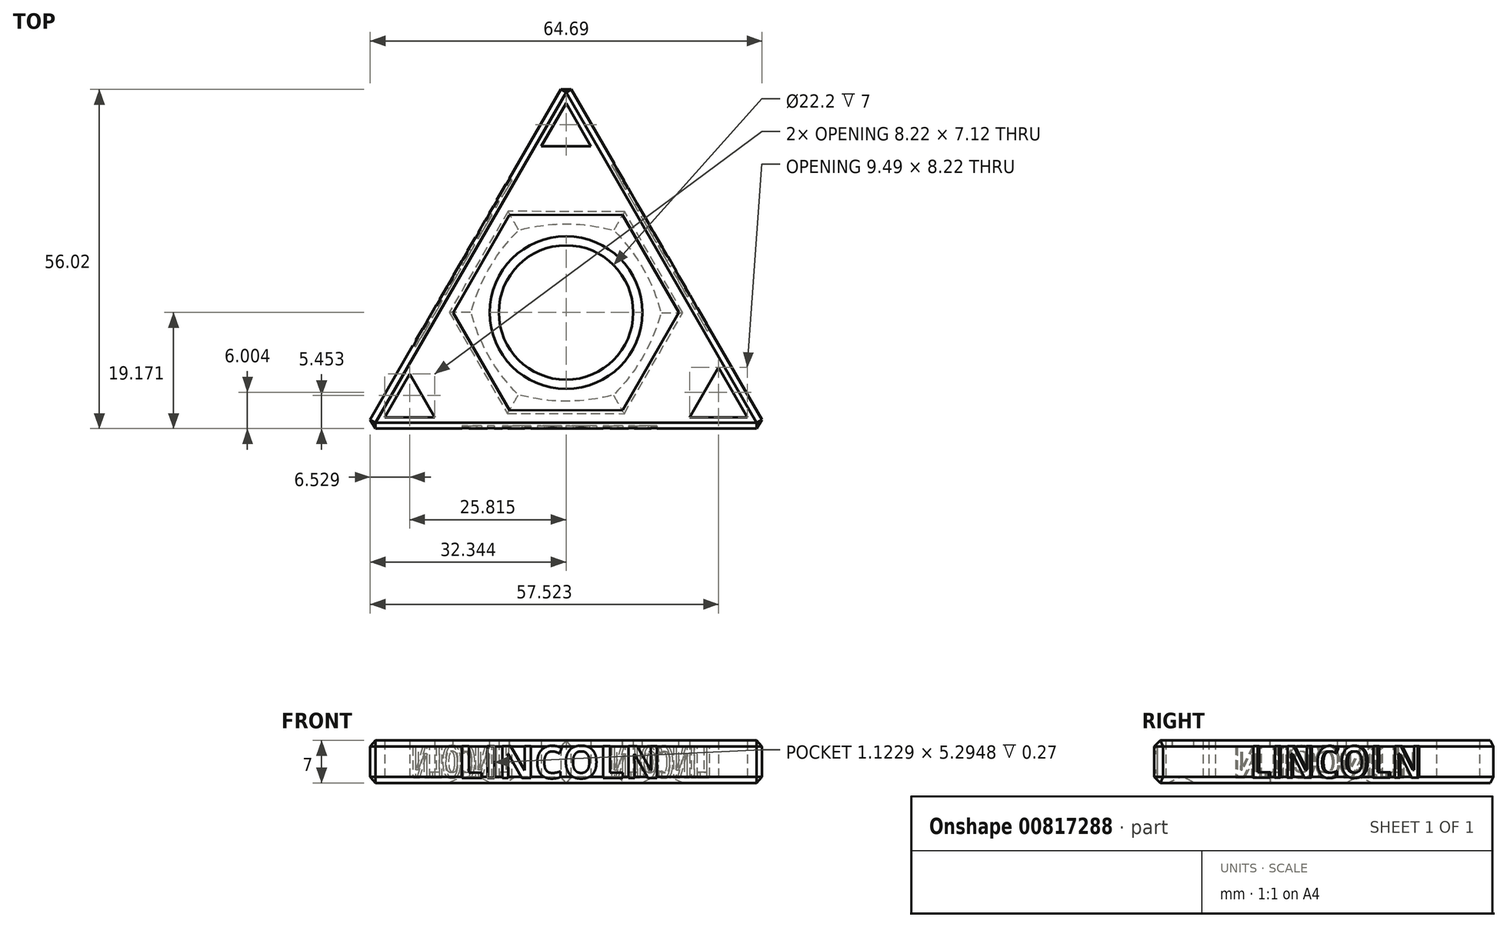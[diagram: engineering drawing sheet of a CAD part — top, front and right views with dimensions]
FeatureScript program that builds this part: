
annotation { "Feature Type Name" : "Feature", "Feature Type Description" : "" }
export const myFeature = defineFeature(function(context is Context, id is Id, definition is map)
    precondition{}
    {
        {
            var Q0;
            Q0=qCreatedBy(makeId("Top.planeOp"),FACE);
            var sketch = newSketch(context, id + "F0", { "sketchPlane" : qUnion([Q0])});
            skLineSegment(sketch, "E0.top", {"start": v(-48.66, -50.6) * mm, "end": v(17.76, -50.6) * mm});
            skLineSegment(sketch, "E1", {"start": v(-48.66, -50.6) * mm, "end": v(-15.45, 6.92) * mm});
            skLineSegment(sketch, "E2", {"start": v(-15.45, 6.92) * mm, "end": v(17.76, -50.6) * mm});
            skCircle(sketch, "E3", {"center": v(-15.45, -31.43) * mm, "radius": 11.1 * mm});
            skPoint(sketch, "E4.start.orphan", {"position": v(-32.05, -21.84) * mm});
            skPoint(sketch, "E5.trimOffspring.end.orphan", {"position": v(-15.45, -50.6) * mm});
            skPoint(sketch, "E6.trimOffspring.end.orphan", {"position": v(0, -21.31) * mm});
            skLineSegment(sketch, "E7.0", {"start": v(-45.37, -48.7) * mm, "end": v(-41.26, -41.59) * mm});
            skLineSegment(sketch, "E8.0", {"start": v(-15.45, 3.12) * mm, "end": v(-11.34, -4) * mm});
            skLineSegment(sketch, "E9.0", {"start": v(-45.37, -48.7) * mm, "end": v(-37.15, -48.7) * mm});
            skLineSegment(sketch, "E10", {"start": v(-37.15, -48.7) * mm, "end": v(-41.26, -41.59) * mm});
            skLineSegment(sketch, "E11", {"start": v(-15.45, -4) * mm, "end": v(-11.34, -4) * mm});
            skLineSegment(sketch, "E12", {"start": v(-15.45, -4) * mm, "end": v(-19.55, -4) * mm});
            skLineSegment(sketch, "E13", {"start": v(7.36, -44.6) * mm, "end": v(9.73, -40.49) * mm});
            skLineSegment(sketch, "E14", {"start": v(7.36, -44.6) * mm, "end": v(4.99, -48.7) * mm});
            skLineSegment(sketch, "E15.trimOffspring", {"start": v(4.99, -48.7) * mm, "end": v(14.48, -48.7) * mm});
            skLineSegment(sketch, "E16.trimOffspring", {"start": v(-19.55, -4) * mm, "end": v(-15.45, 3.12) * mm});
            skLineSegment(sketch, "E17.trimOffspring", {"start": v(9.73, -40.49) * mm, "end": v(14.48, -48.7) * mm});
            skSolve(sketch);
        }
        {
            var Q0;
            Q0=makeQuery(id+"F0.imprint","IMPRINT",FACE,{"disambiguationData":[TD([[makeQuery(id+"F0.imprint","IMPRINT",EDGE,{"derivedFrom":sQuery(id+"F0.wireOp",EDGE,"E0.top")}),1.0]])]});
            extrude(context, id + "F1", {"entities" : qUnion([Q0]), "depth" : 7 * mm, "offsetDistance" : 25 * mm});
        }
        {
            var Q0;
            Q0=makeQuery(id+"F1.opExtrude","SWEPT_FACE",FACE,{"disambiguationData":[OSD([sQuery(id+"F0.wireOp",EDGE,"E0.top")])]});
            var Q1;
            Q1=makeQuery(id+"F1.opExtrude","SWEPT_FACE",FACE,{"disambiguationData":[OSD([sQuery(id+"F0.wireOp",EDGE,"E2")])]});
            var Q2;
            Q2=makeQuery(id+"F1.opExtrude","SWEPT_FACE",FACE,{"disambiguationData":[OSD([sQuery(id+"F0.wireOp",EDGE,"E1")])]});
            chamfer(context, id + "F2", {"entities" : qUnion([Q0, Q1, Q2]), "width" : 1 * mm, "tangentPropagation" : true});
        }
        {
            var Q0;
            Q0=makeQuery(id+"F1.opExtrude","SWEPT_FACE",FACE,{"disambiguationData":[OSD([sQuery(id+"F0.wireOp",EDGE,"E1")])]});
            var sketch = newSketch(context, id + "F3", { "sketchPlane" : qUnion([Q0])});
            skText(sketch, "E18", { "text": "LINCOLN", "fontName": "OpenSans-Bold.ttf"});
            const initialGuessF3  = {"E18": [0.0198, 0.00085, 1, 0, 0.00528]};
            skSetInitialGuess(sketch, initialGuessF3);
            skSolve(sketch);
        }
        {
            var Q0;
            Q0 = qSketchRegion(id + "F3", true);
            extrude(context, id + "F4", {"entities" : qUnion([Q0]), "operationType" : NewBodyOperationType.REMOVE, "oppositeDirection" : true, "depth" : 0.5 * mm, "offsetDistance" : 25 * mm});
        }
        {
            var Q0;
            Q0=makeQuery(id+"F1.opExtrude","SWEPT_FACE",FACE,{"disambiguationData":[OSD([sQuery(id+"F0.wireOp",EDGE,"E0.top")])]});
            var sketch = newSketch(context, id + "F5", { "sketchPlane" : qUnion([Q0])});
            skText(sketch, "E19", { "text": "LINCOLN", "fontName": "OpenSans-Bold.ttf"});
            const initialGuessF5  = {"E19": [-0.0333, 0.00077, 1, 0, 0.00534]};
            skSetInitialGuess(sketch, initialGuessF5);
            skSolve(sketch);
        }
        {
            var Q0;
            Q0 = qSketchRegion(id + "F5", true);
            extrude(context, id + "F6", {"entities" : qUnion([Q0]), "operationType" : NewBodyOperationType.REMOVE, "oppositeDirection" : true, "depth" : 0.5 * mm, "offsetDistance" : 25 * mm});
        }
        {
            var Q0;
            Q0=makeQuery(id+"F1.opExtrude","SWEPT_FACE",FACE,{"disambiguationData":[OSD([sQuery(id+"F0.wireOp",EDGE,"E2")])]});
            var sketch = newSketch(context, id + "F7", { "sketchPlane" : qUnion([Q0])});
            skText(sketch, "E20", { "text": "LINCOLN", "fontName": "OpenSans-Bold.ttf"});
            const initialGuessF7  = {"E20": [-0.0344, 0.00085, 1, 0, 0.00524]};
            skSetInitialGuess(sketch, initialGuessF7);
            skSolve(sketch);
        }
        {
            var Q0;
            Q0 = qSketchRegion(id + "F7", true);
            extrude(context, id + "F8", {"entities" : qUnion([Q0]), "operationType" : NewBodyOperationType.REMOVE, "oppositeDirection" : true, "depth" : 0.5 * mm, "offsetDistance" : 25 * mm});
        }
        {
            var Q0;
            Q0=makeQuery(id+"F1.opExtrude","CAP_FACE",FACE,{"disambiguationData":[OSD([sQuery(id+"F0.wireOp",EDGE,"E0.top"),sQuery(id+"F0.wireOp",EDGE,"E1"),sQuery(id+"F0.wireOp",EDGE,"E2"),sQuery(id+"F0.wireOp",EDGE,"E3"),sQuery(id+"F0.wireOp",EDGE,"E7.0"),sQuery(id+"F0.wireOp",EDGE,"E8.0"),sQuery(id+"F0.wireOp",EDGE,"E9.0"),sQuery(id+"F0.wireOp",EDGE,"E10"),sQuery(id+"F0.wireOp",EDGE,"E11"),sQuery(id+"F0.wireOp",EDGE,"E12"),sQuery(id+"F0.wireOp",EDGE,"E13"),sQuery(id+"F0.wireOp",EDGE,"E14"),sQuery(id+"F0.wireOp",EDGE,"E15.trimOffspring"),sQuery(id+"F0.wireOp",EDGE,"E16.trimOffspring"),sQuery(id+"F0.wireOp",EDGE,"E17.trimOffspring")])],"isStart":false});
            var sketch = newSketch(context, id + "F9", { "sketchPlane" : qUnion([Q0])});
            skCircle(sketch, "E21.0", {"center": v(-15.45, -31.43) * mm, "radius": 12.6 * mm});
            skCircle(sketch, "E22.cCircle", {"center": v(-15.45, -31.43) * mm, "radius": 18.63 * mm, "construction": true});
            skLineSegment(sketch, "E22.0", {"start": v(-6.16, -15.28) * mm, "end": v(3.18, -31.4) * mm});
            skLineSegment(sketch, "E22.1", {"start": v(3.18, -31.4) * mm, "end": v(-6.1, -47.54) * mm});
            skLineSegment(sketch, "E22.2", {"start": v(-6.1, -47.54) * mm, "end": v(-24.73, -47.58) * mm});
            skLineSegment(sketch, "E22.3", {"start": v(-24.73, -47.58) * mm, "end": v(-34.08, -31.47) * mm});
            skLineSegment(sketch, "E22.4", {"start": v(-34.08, -31.47) * mm, "end": v(-24.8, -15.31) * mm});
            skLineSegment(sketch, "E22.5", {"start": v(-24.8, -15.31) * mm, "end": v(-6.16, -15.28) * mm});
            skSolve(sketch);
        }
        {
            var Q0;
            Q0=makeQuery(id+"F9.imprint","IMPRINT",FACE,{"disambiguationData":[TD([[makeQuery(id+"F9.imprint","IMPRINT",EDGE,{"derivedFrom":sQuery(id+"F9.wireOp",EDGE,"E21.0")}),-1.0]])]});
            extrude(context, id + "F10", {"entities" : qUnion([Q0]), "operationType" : NewBodyOperationType.REMOVE, "oppositeDirection" : true, "depth" : 1 * mm, "offsetDistance" : 25 * mm});
        }
        {
            var Q0;
            Q0=makeQuery(id+"F1.opExtrude","CAP_FACE",FACE,{"disambiguationData":[OSD([sQuery(id+"F0.wireOp",EDGE,"E0.top"),sQuery(id+"F0.wireOp",EDGE,"E1"),sQuery(id+"F0.wireOp",EDGE,"E2"),sQuery(id+"F0.wireOp",EDGE,"E3"),sQuery(id+"F0.wireOp",EDGE,"E7.0"),sQuery(id+"F0.wireOp",EDGE,"E8.0"),sQuery(id+"F0.wireOp",EDGE,"E9.0"),sQuery(id+"F0.wireOp",EDGE,"E10"),sQuery(id+"F0.wireOp",EDGE,"E11"),sQuery(id+"F0.wireOp",EDGE,"E12"),sQuery(id+"F0.wireOp",EDGE,"E13"),sQuery(id+"F0.wireOp",EDGE,"E14"),sQuery(id+"F0.wireOp",EDGE,"E15.trimOffspring"),sQuery(id+"F0.wireOp",EDGE,"E16.trimOffspring"),sQuery(id+"F0.wireOp",EDGE,"E17.trimOffspring")])],"isStart":true});
            var sketch = newSketch(context, id + "F11", { "sketchPlane" : qUnion([Q0])});
            skCircle(sketch, "E23.0", {"center": v(-15.45, 31.43) * mm, "radius": 12.6 * mm});
            skCircle(sketch, "E24.cCircle", {"center": v(-15.45, 31.43) * mm, "radius": 19.26 * mm, "construction": true});
            skLineSegment(sketch, "E24.0", {"start": v(-5.86, 48.14) * mm, "end": v(3.82, 31.48) * mm});
            skLineSegment(sketch, "E24.1", {"start": v(3.82, 31.48) * mm, "end": v(-5.77, 14.77) * mm});
            skLineSegment(sketch, "E24.2", {"start": v(-5.77, 14.77) * mm, "end": v(-25.04, 14.72) * mm});
            skLineSegment(sketch, "E24.3", {"start": v(-25.04, 14.72) * mm, "end": v(-34.7, 31.38) * mm});
            skLineSegment(sketch, "E24.4", {"start": v(-34.7, 31.38) * mm, "end": v(-25.12, 48.09) * mm});
            skLineSegment(sketch, "E24.5", {"start": v(-25.12, 48.09) * mm, "end": v(-5.86, 48.14) * mm});
            skSolve(sketch);
        }
        {
            var Q0;
            Q0=makeQuery(id+"F11.imprint","IMPRINT",FACE,{"disambiguationData":[TD([[makeQuery(id+"F11.imprint","IMPRINT",EDGE,{"derivedFrom":sQuery(id+"F11.wireOp",EDGE,"E23.0")}),-1.0]])]});
            extrude(context, id + "F12", {"entities" : qUnion([Q0]), "operationType" : NewBodyOperationType.REMOVE, "oppositeDirection" : true, "depth" : 1 * mm, "offsetDistance" : 25 * mm});
        }
        {
            var Q0;
            Q0=makeQuery(id+"F12.boolean.opBoolean","COPY",FACE,{"derivedFrom":makeQuery(id+"F12.opExtrude","CAP_FACE",FACE,{"disambiguationData":[OSD([sQuery(id+"F11.wireOp",EDGE,"E23.0"),sQuery(id+"F11.wireOp",EDGE,"E24.0"),sQuery(id+"F11.wireOp",EDGE,"E24.1"),sQuery(id+"F11.wireOp",EDGE,"E24.2"),sQuery(id+"F11.wireOp",EDGE,"E24.3"),sQuery(id+"F11.wireOp",EDGE,"E24.4"),sQuery(id+"F11.wireOp",EDGE,"E24.5")])],"isStart":false})});
            fillet(context, id + "F13", {"entities" : qUnion([Q0]), "radius" : 5 * mm, "tangentPropagation" : true, "allowEdgeOverflow" : false});
        }
    });
